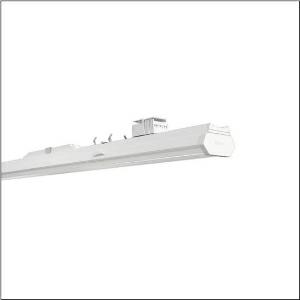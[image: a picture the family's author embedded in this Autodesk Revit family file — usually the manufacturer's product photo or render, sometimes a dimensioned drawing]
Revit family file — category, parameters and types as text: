
# Revit family: licross_r__21_protected_mo_52td12dn4a5g3s_ad63
name_source: partatom
category: Lighting Fixtures
units: mm (PartAtom-declared; Revit-internal decimal feet)

## family parameters
Cut with Voids When Loaded = No
Host = Face
Light Source = No
Part Type = Normal
Room Calculation Point = No
Round Connector Dimension = Use Diameter
Shared = No

## types (1)
- --- (1 x LED, 940 lm, 6.8 W, 4000K)
    Apparent Load = 7 VA
    CIE Flux Codes = 73 92 98 99 100
    Color Rendering = 80
    Color Temperature = 4000K
    Default Elevation = 1800 mm
    Description = Licross® 21 Protected MO, luminaire insert, of sheet steel, galvanised, coil coated, white, length: 1.500mm, width: 90mm, height: 103mm, LED rated luminous flux: 10.700lm, light colour: 840, control gear: DALI 2 (for two DALI lines), with plug, 6-pole, with phase selection, for trunking rail, 14-core, mains connection: 220..240V, AC, 50/60Hz, rated input power: 66W, for trunking rail, 14-core, halogen-free wiring, for emergency light function, converter,control gear: single battery element, battery: LiFePO4, 9Ah, primary light control with lens, of plastic, primary optical cover: cover, of PMMA, light emission: direct distribution, primary light characteristic: symmetric, protection rating (complete): IP54, insulation class (complete): insulation class I (protective earthing), certification: CE, UKCA, protection symbol: D if used in an environment with non-conductive dust loads with corresponding accessories, impact resistance: IK06, permissible ambient temperature for indoor applications: +5..+35°C, standard: EN 60598-2-22, LABS conformity tested according to VDMA 24364:2018-05, reducing of maximum allowable ambient temperature of 5°C with ceiling mounting, corresponds to IFS (International Featured Standards) requirements for safety and quality in the food industry, packaging unit: 1 piece
    Height = 92 mm
    Lamp = 1 x LED
    Lamp Light Flux = 940 lm
    Lamp Power = 6.8 W
    Lamp count = 1
    Length = 1500 mm
    Luminous efficacy = 138 lm/W
    Manufacturer = Siteco
    ModVariant = No
    Model = 52TD12DN4A5G3S
    Mounting Place = Ceiling
    Mounting Type = Pendant
    Number of Poles = 1
    OnlyDefault = Yes
    Power Factor = 1
    Product Name = Licross® 21 Protected MO
    Product group = luminaire insert
    ProductGroupID = 902
    Protection Class = Protection class I
    Protection Degree = IP 54
    RLX_Detail_Level = 1
    RLX_Emergency_Light_Flux = 0 lm
    RLX_Emergency_Type = 0
    RLX_Emergency_Type_DB = No
    RlxData = <blob elided: 24765 chars, md5=d8e7bf9a>
    Socket = socket
    Standby Power = 0 W
    System Light Flux = 940 lm
    System Power = 7 W
    Type Comments = : emergency light operation: 3 h
    Type Image = l_1256148.jpg
    URL = http://relux.com
    VarID = @adj_110936
    Voltage = 0 V
    Weight = 0.00 kg
    Width = 88 mm

## geometry (parser evidence)
native form markers: Blend x4, Sweep x11
no freeform markers — native parametric forms only
